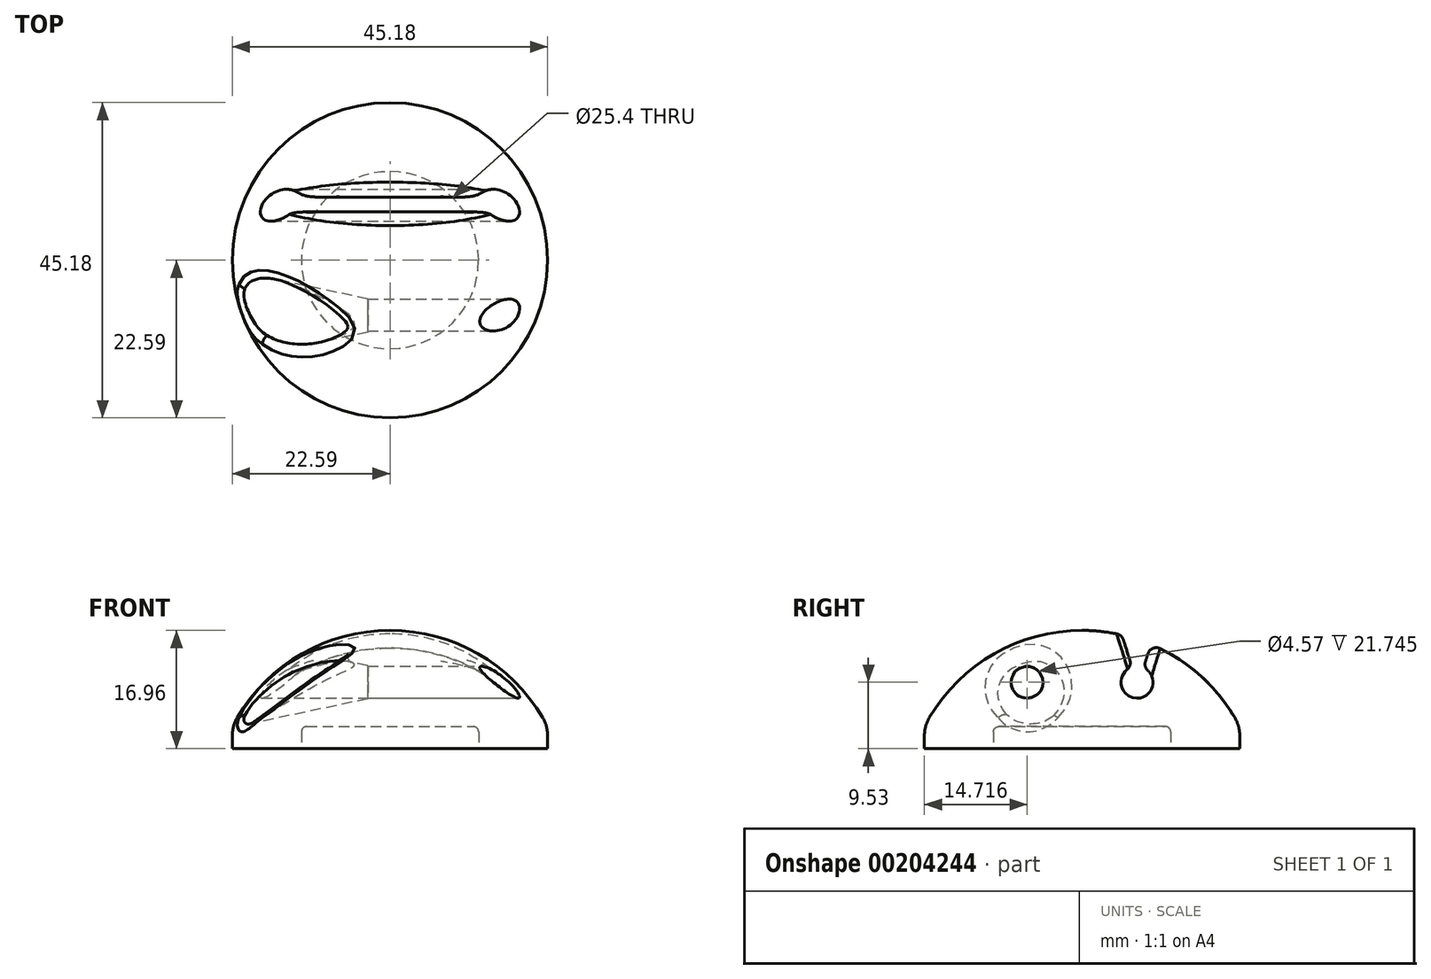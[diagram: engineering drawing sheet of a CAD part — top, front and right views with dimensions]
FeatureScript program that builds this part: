
annotation { "Feature Type Name" : "Feature", "Feature Type Description" : "" }
export const myFeature = defineFeature(function(context is Context, id is Id, definition is map)
    precondition{}
    {
        {
            var Q0;
            Q0=qCreatedBy(makeId("Right.planeOp"),FACE);
            var sketch = newSketch(context, id + "F0", { "sketchPlane" : qUnion([Q0])});
            skLineSegment(sketch, "E0", {"start": v(0, 0) * mm, "end": v(0, 13.78) * mm});
            skArc(sketch, "E1", {"start": v(22.59, 0) * mm, "mid": v(13.23, 10.06) * mm, "end": v(0, 13.78) * mm});
            skLineSegment(sketch, "E2", {"start": v(0, 0) * mm, "end": v(22.59, 0) * mm});
            skLineSegment(sketch, "E3", {"start": v(0, -11.62) * mm, "end": v(0, 45.48) * mm, "construction": true});
            skSolve(sketch);
        }
        {
            var Q0;
            Q0 = qSketchRegion(id + "F0", true);
            var Q1;
            Q1=sQuery(id+"F0.wireOp",EDGE,"E3");
            revolve(context, id + "F1", {"entities" : qUnion([Q0]), "axis" : qUnion([Q1]), "revolveType" : RevolveType.FULL});
        }
        {
            var Q0;
            Q0=makeQuery(id+"F1.opRevolve","SWEPT_FACE",FACE,{"disambiguationData":[OSD([sQuery(id+"F0.wireOp",EDGE,"E2")])]});
            extrude(context, id + "F2", {"entities" : qUnion([Q0]), "operationType" : NewBodyOperationType.ADD, "depth" : 3.17 * mm});
        }
        {
            var Q0;
            {var subQ0=sQuery(id+"F0.wireOp",EDGE,"E2");var subQ1=sQuery(id+"F0.wireOp",EDGE,"E1");Q0=makeQuery(id+"F2.boolean.opBoolean","MERGE",EDGE,{"derivedFrom":[makeQuery(id+"F1.opRevolve","SWEPT_EDGE",EDGE,{"disambiguationData":[OSD([subQ1,subQ0])]}),makeQuery(id+"F2.opExtrude","CAP_EDGE",EDGE,{"disambiguationData":[OSD([subQ1,subQ0])],"isStart":true})]});}
            fillet(context, id + "F3", {"entities" : qUnion([Q0]), "radius" : 5.08 * mm, "tangentPropagation" : true, "allowEdgeOverflow" : false});
        }
        {
            var Q0;
            Q0=qCreatedBy(makeId("Right.planeOp"),FACE);
            var sketch = newSketch(context, id + "F4", { "sketchPlane" : qUnion([Q0])});
            skCircle(sketch, "E4", {"center": v(-7.87, 6.35) * mm, "radius": 2.29 * mm});
            skCircle(sketch, "E5.MirrorC", {"center": v(7.87, 6.35) * mm, "radius": 2.29 * mm});
            skSolve(sketch);
        }
        {
            var Q0;
            Q0 = qSketchRegion(id + "F4", true);
            extrude(context, id + "F5", {"entities" : qUnion([Q0]), "operationType" : NewBodyOperationType.REMOVE, "endBound" : BoundingType.UP_TO_NEXT, "oppositeDirection" : true, "depth" : 25.4 * mm, "hasSecondDirection" : true, "secondDirectionBound" : SecondDirectionBoundingType.UP_TO_NEXT, "secondDirectionOppositeDirection" : false, "secondDirectionDepth" : 25.4 * mm});
        }
        {
            var Q0;
            Q0=qCreatedBy(makeId("Front.planeOp"),FACE);
            cPlane(context, id + "F6", {"entities" : qUnion([Q0]), "cplaneType" : CPlaneType.OFFSET, "offset" : 7.94 * mm, "width" : 152.4 * mm, "height" : 152.4 * mm});
        }
        {
            var Q0;
            Q0=qCreatedBy(id+"F6.planeOp",FACE);
            var sketch = newSketch(context, id + "F7", { "sketchPlane" : qUnion([Q0])});
            skLineSegment(sketch, "E6", {"start": v(-26.76, 6.35) * mm, "end": v(-3.17, 6.35) * mm, "construction": true});
            skLineSegment(sketch, "E7", {"start": v(-25.4, 6.35) * mm, "end": v(-25.4, 13.46) * mm});
            skLineSegment(sketch, "E8", {"start": v(-25.4, 6.35) * mm, "end": v(-3.18, 6.35) * mm});
            skPoint(sketch, "E9.end.orphan", {"position": v(-25.4, -0.76) * mm});
            skLineSegment(sketch, "E10", {"start": v(-25.4, 13.46) * mm, "end": v(-3.17, 8.73) * mm});
            skLineSegment(sketch, "E11", {"start": v(-3.17, 8.73) * mm, "end": v(-3.17, 6.35) * mm});
            skLineSegment(sketch, "E12.trimOffspring", {"start": v(0, 6.35) * mm, "end": v(34.7, 6.35) * mm, "construction": true});
            skSolve(sketch);
        }
        {
            var Q0;
            Q0 = qSketchRegion(id + "F7", true);
            var Q1;
            Q1=sQuery(id+"F7.wireOp",EDGE,"E6");
            revolve(context, id + "F8", {"operationType" : NewBodyOperationType.REMOVE, "entities" : qUnion([Q0]), "axis" : qUnion([Q1]), "revolveType" : RevolveType.FULL, "oppositeDirection" : true});
        }
        {
            var Q0;
            Q0=qCreatedBy(makeId("Right.planeOp"),FACE);
            var sketch = newSketch(context, id + "F9", { "sketchPlane" : qUnion([Q0])});
            skLineSegment(sketch, "E13", {"start": v(10.36, 13.39) * mm, "end": v(7.99, 5.88) * mm});
            skLineSegment(sketch, "E14", {"start": v(7.99, 5.88) * mm, "end": v(5.62, 13.39) * mm});
            skLineSegment(sketch, "E15", {"start": v(10.36, 13.39) * mm, "end": v(5.62, 13.39) * mm});
            skSolve(sketch);
        }
        {
            var Q0;
            Q0 = qSketchRegion(id + "F9", true);
            extrude(context, id + "F10", {"entities" : qUnion([Q0]), "operationType" : NewBodyOperationType.REMOVE, "endBound" : BoundingType.THROUGH_ALL, "oppositeDirection" : true, "depth" : 25.4 * mm, "hasSecondDirection" : true, "secondDirectionBound" : SecondDirectionBoundingType.THROUGH_ALL, "secondDirectionOppositeDirection" : false, "secondDirectionDepth" : 25.4 * mm});
        }
        {
            var Q0;
            Q0=makeQuery(id+"F10.boolean.opBoolean","INTERSECT",EDGE,{"derivedFrom":[makeQuery(id+"F1.opRevolve","SWEPT_FACE",FACE,{"disambiguationData":[OSD([sQuery(id+"F0.wireOp",EDGE,"E1")])]}),makeQuery(id+"F10.opExtrude","SWEPT_FACE",FACE,{"disambiguationData":[OSD([sQuery(id+"F9.wireOp",EDGE,"E13")])]})]});
            var Q1;
            Q1=makeQuery(id+"F10.boolean.opBoolean","INTERSECT",EDGE,{"derivedFrom":[makeQuery(id+"F1.opRevolve","SWEPT_FACE",FACE,{"disambiguationData":[OSD([sQuery(id+"F0.wireOp",EDGE,"E1")])]}),makeQuery(id+"F10.opExtrude","SWEPT_FACE",FACE,{"disambiguationData":[OSD([sQuery(id+"F9.wireOp",EDGE,"E14")])]})]});
            var Q2;
            {var subQ0=sQuery(id+"F0.wireOp",EDGE,"E1");var subQ1=makeQuery(id+"F1.opRevolve","SWEPT_FACE",FACE,{"disambiguationData":[OSD([subQ0])]});var subQ2=makeQuery(id+"FQL3Fsu7UHnpzhg_1.1.F8.opRevolve","SWEPT_FACE",FACE,{"disambiguationData":[OSD([sQuery(id+"FQL3Fsu7UHnpzhg_1.1.F7.wireOp",EDGE,"E10")])]});Q2=makeQuery(id+"F10.boolean.opBoolean","SPLIT",EDGE,{"disambiguationData":[TD([makeQuery(id+"F10.opExtrude","SWEPT_FACE",FACE,{"disambiguationData":[OSD([sQuery(id+"F9.wireOp",EDGE,"E13")])]})])],"derivedFrom":makeQuery(id+"FQL3Fsu7UHnpzhg_1.1.F8.boolean.opBoolean","INTERSECT",EDGE,{"derivedFrom":[subQ1,subQ2]})});}
            var Q3;
            {var subQ0=sQuery(id+"F0.wireOp",EDGE,"E1");var subQ1=makeQuery(id+"F1.opRevolve","SWEPT_FACE",FACE,{"disambiguationData":[OSD([subQ0])]});var subQ2=makeQuery(id+"FQL3Fsu7UHnpzhg_1.1.FvJgrAM00djZwU5_1.1.F8.opRevolve","SWEPT_FACE",FACE,{"disambiguationData":[OSD([sQuery(id+"FQL3Fsu7UHnpzhg_1.1.FvJgrAM00djZwU5_1.1.F7.wireOp",EDGE,"E10")])]});Q3=makeQuery(id+"F10.boolean.opBoolean","SPLIT",EDGE,{"disambiguationData":[TD([makeQuery(id+"F10.opExtrude","SWEPT_FACE",FACE,{"disambiguationData":[OSD([sQuery(id+"F9.wireOp",EDGE,"E13")])]})])],"derivedFrom":makeQuery(id+"FQL3Fsu7UHnpzhg_1.1.FvJgrAM00djZwU5_1.1.F8.boolean.opBoolean","INTERSECT",EDGE,{"derivedFrom":[subQ1,subQ2]})});}
            var Q4;
            Q4=makeQuery(id+"F10.boolean.opBoolean","INTERSECT",EDGE,{"derivedFrom":[makeQuery(id+"F5.boolean.opBoolean","COPY",FACE,{"derivedFrom":makeQuery(id+"F5.opExtrude","SWEPT_FACE",FACE,{"disambiguationData":[OSD([sQuery(id+"F4.wireOp",EDGE,"E5.MirrorC")])]})}),makeQuery(id+"F10.opExtrude","SWEPT_FACE",FACE,{"disambiguationData":[OSD([sQuery(id+"F9.wireOp",EDGE,"E13")])]})]});
            var Q5;
            Q5=makeQuery(id+"F10.boolean.opBoolean","INTERSECT",EDGE,{"derivedFrom":[makeQuery(id+"F5.boolean.opBoolean","COPY",FACE,{"derivedFrom":makeQuery(id+"F5.opExtrude","SWEPT_FACE",FACE,{"disambiguationData":[OSD([sQuery(id+"F4.wireOp",EDGE,"E5.MirrorC")])]})}),makeQuery(id+"F10.opExtrude","SWEPT_FACE",FACE,{"disambiguationData":[OSD([sQuery(id+"F9.wireOp",EDGE,"E14")])]})]});
            var Q6;
            {var subQ0=sQuery(id+"F0.wireOp",EDGE,"E1");var subQ1=makeQuery(id+"F1.opRevolve","SWEPT_FACE",FACE,{"disambiguationData":[OSD([subQ0])]});var subQ2=makeQuery(id+"F8.opRevolve","SWEPT_FACE",FACE,{"disambiguationData":[OSD([sQuery(id+"F7.wireOp",EDGE,"E10")])]});Q6=makeQuery(id+"Fyp1GfY2Lm32MM5_1.1.F10.boolean.opBoolean","SPLIT",EDGE,{"disambiguationData":[TD([makeQuery(id+"Fyp1GfY2Lm32MM5_1.1.F10.opExtrude","SWEPT_FACE",FACE,{"disambiguationData":[OSD([sQuery(id+"Fyp1GfY2Lm32MM5_1.1.F9.wireOp",EDGE,"E14")])]})])],"derivedFrom":makeQuery(id+"F8.boolean.opBoolean","INTERSECT",EDGE,{"derivedFrom":[subQ1,subQ2]})});}
            var Q7;
            {var subQ0=sQuery(id+"F0.wireOp",EDGE,"E1");var subQ1=makeQuery(id+"F1.opRevolve","SWEPT_FACE",FACE,{"disambiguationData":[OSD([subQ0])]});var subQ2=makeQuery(id+"FvJgrAM00djZwU5_1.1.F8.opRevolve","SWEPT_FACE",FACE,{"disambiguationData":[OSD([sQuery(id+"FvJgrAM00djZwU5_1.1.F7.wireOp",EDGE,"E10")])]});Q7=makeQuery(id+"Fyp1GfY2Lm32MM5_1.1.F10.boolean.opBoolean","SPLIT",EDGE,{"disambiguationData":[TD([makeQuery(id+"Fyp1GfY2Lm32MM5_1.1.F10.opExtrude","SWEPT_FACE",FACE,{"disambiguationData":[OSD([sQuery(id+"Fyp1GfY2Lm32MM5_1.1.F9.wireOp",EDGE,"E13")])]})])],"derivedFrom":makeQuery(id+"FvJgrAM00djZwU5_1.1.F8.boolean.opBoolean","INTERSECT",EDGE,{"derivedFrom":[subQ1,subQ2]})});}
            var Q8;
            {var subQ0=sQuery(id+"F0.wireOp",EDGE,"E1");Q8=makeQuery(id+"Fyp1GfY2Lm32MM5_1.1.F10.boolean.opBoolean","INTERSECT",EDGE,{"derivedFrom":[makeQuery(id+"F10.boolean.opBoolean","SPLIT",FACE,{"disambiguationData":[TD([makeQuery(id+"F8.boolean.opBoolean","COPY",FACE,{"derivedFrom":makeQuery(id+"F8.opRevolve","SWEPT_FACE",FACE,{"disambiguationData":[OSD([sQuery(id+"F7.wireOp",EDGE,"E10")])]})})])],"derivedFrom":makeQuery(id+"F1.opRevolve","SWEPT_FACE",FACE,{"disambiguationData":[OSD([subQ0])]})}),makeQuery(id+"Fyp1GfY2Lm32MM5_1.1.F10.opExtrude","SWEPT_FACE",FACE,{"disambiguationData":[OSD([sQuery(id+"Fyp1GfY2Lm32MM5_1.1.F9.wireOp",EDGE,"E13")])]})]});}
            var Q9;
            {var subQ0=sQuery(id+"F0.wireOp",EDGE,"E1");Q9=makeQuery(id+"Fyp1GfY2Lm32MM5_1.1.F10.boolean.opBoolean","INTERSECT",EDGE,{"derivedFrom":[makeQuery(id+"F10.boolean.opBoolean","SPLIT",FACE,{"disambiguationData":[TD([makeQuery(id+"F8.boolean.opBoolean","COPY",FACE,{"derivedFrom":makeQuery(id+"F8.opRevolve","SWEPT_FACE",FACE,{"disambiguationData":[OSD([sQuery(id+"F7.wireOp",EDGE,"E10")])]})})])],"derivedFrom":makeQuery(id+"F1.opRevolve","SWEPT_FACE",FACE,{"disambiguationData":[OSD([subQ0])]})}),makeQuery(id+"Fyp1GfY2Lm32MM5_1.1.F10.opExtrude","SWEPT_FACE",FACE,{"disambiguationData":[OSD([sQuery(id+"Fyp1GfY2Lm32MM5_1.1.F9.wireOp",EDGE,"E14")])]})]});}
            var Q10;
            Q10=makeQuery(id+"Fyp1GfY2Lm32MM5_1.1.F10.boolean.opBoolean","INTERSECT",EDGE,{"derivedFrom":[makeQuery(id+"F5.boolean.opBoolean","COPY",FACE,{"derivedFrom":makeQuery(id+"F5.opExtrude","SWEPT_FACE",FACE,{"disambiguationData":[OSD([sQuery(id+"F4.wireOp",EDGE,"E4")])]})}),makeQuery(id+"Fyp1GfY2Lm32MM5_1.1.F10.opExtrude","SWEPT_FACE",FACE,{"disambiguationData":[OSD([sQuery(id+"Fyp1GfY2Lm32MM5_1.1.F9.wireOp",EDGE,"E13")])]})]});
            var Q11;
            Q11=makeQuery(id+"Fyp1GfY2Lm32MM5_1.1.F10.boolean.opBoolean","INTERSECT",EDGE,{"derivedFrom":[makeQuery(id+"F5.boolean.opBoolean","COPY",FACE,{"derivedFrom":makeQuery(id+"F5.opExtrude","SWEPT_FACE",FACE,{"disambiguationData":[OSD([sQuery(id+"F4.wireOp",EDGE,"E4")])]})}),makeQuery(id+"Fyp1GfY2Lm32MM5_1.1.F10.opExtrude","SWEPT_FACE",FACE,{"disambiguationData":[OSD([sQuery(id+"Fyp1GfY2Lm32MM5_1.1.F9.wireOp",EDGE,"E14")])]})]});
            fillet(context, id + "F11", {"entities" : qUnion([Q0, Q1, Q2, Q3, Q4, Q5, Q6, Q7, Q8, Q9, Q10, Q11]), "radius" : 1.27 * mm, "tangentPropagation" : true, "allowEdgeOverflow" : false});
        }
        {
            var Q0;
            Q0=makeQuery(id+"F2.opExtrude","CAP_FACE",FACE,{"disambiguationData":[OSD([sQuery(id+"F0.wireOp",EDGE,"E2")])],"isStart":false});
            var sketch = newSketch(context, id + "F12", { "sketchPlane" : qUnion([Q0])});
            skCircle(sketch, "E16", {"center": v(0, 0) * mm, "radius": 12.7 * mm});
            skSolve(sketch);
        }
        {
            var Q0;
            Q0 = qSketchRegion(id + "F12", true);
            extrude(context, id + "F13", {"entities" : qUnion([Q0]), "operationType" : NewBodyOperationType.REMOVE, "oppositeDirection" : true, "depth" : 3.17 * mm});
        }
        {
            var Q0;
            Q0=makeQuery(id+"F13.boolean.opBoolean","COPY",EDGE,{"derivedFrom":makeQuery(id+"F13.opExtrude","CAP_EDGE",EDGE,{"disambiguationData":[OSD([sQuery(id+"F12.wireOp",EDGE,"E16")])],"isStart":false})});
            fillet(context, id + "F14", {"entities" : qUnion([Q0]), "radius" : 0.76 * mm, "tangentPropagation" : true, "allowEdgeOverflow" : false});
        }
    });
